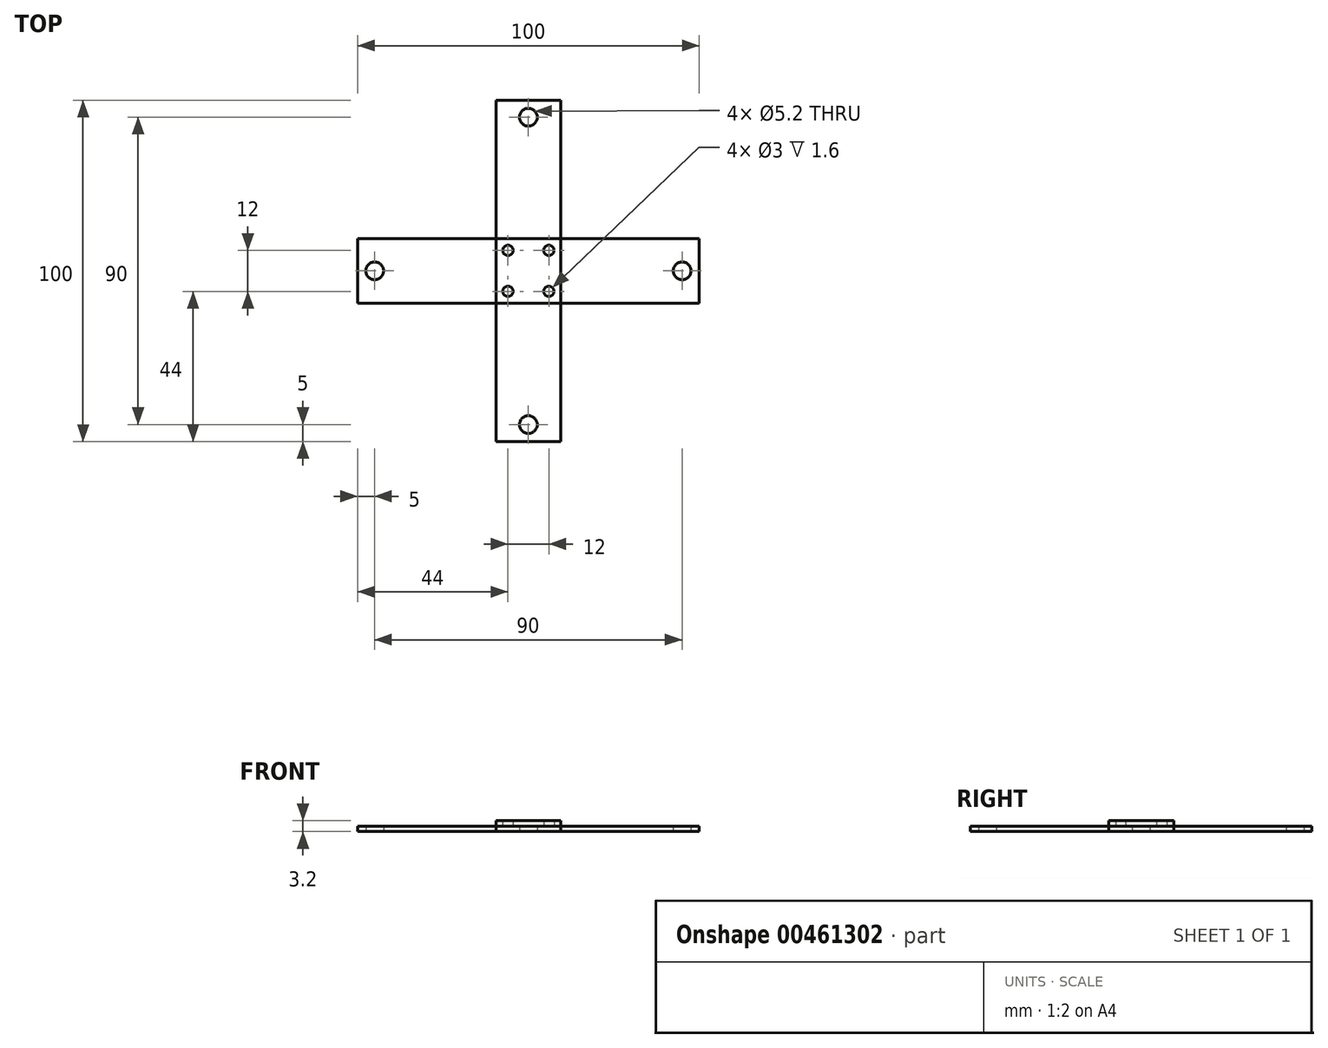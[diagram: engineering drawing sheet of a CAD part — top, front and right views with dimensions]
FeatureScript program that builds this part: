
annotation { "Feature Type Name" : "Feature", "Feature Type Description" : "" }
export const myFeature = defineFeature(function(context is Context, id is Id, definition is map)
    precondition{}
    {
        {
            var Q0;
            Q0=qCreatedBy(makeId("Top.planeOp"),FACE);
            var sketch = newSketch(context, id + "F0", { "sketchPlane" : qUnion([Q0])});
            skLineSegment(sketch, "E0", {"start": v(-9.5, 50) * mm, "end": v(9.5, 50) * mm});
            skLineSegment(sketch, "E1", {"start": v(9.5, 50) * mm, "end": v(9.5, 9.5) * mm});
            skLineSegment(sketch, "E2", {"start": v(9.5, 9.5) * mm, "end": v(50, 9.5) * mm});
            skLineSegment(sketch, "E3", {"start": v(50, 9.5) * mm, "end": v(50, -9.5) * mm});
            skLineSegment(sketch, "E4", {"start": v(50, -9.5) * mm, "end": v(9.5, -9.5) * mm});
            skLineSegment(sketch, "E5", {"start": v(9.5, -9.5) * mm, "end": v(9.5, -50) * mm});
            skLineSegment(sketch, "E6", {"start": v(9.5, -50) * mm, "end": v(-9.5, -50) * mm});
            skLineSegment(sketch, "E7", {"start": v(-9.5, -50) * mm, "end": v(-9.5, -9.5) * mm});
            skLineSegment(sketch, "E8", {"start": v(-9.5, -9.5) * mm, "end": v(-50, -9.5) * mm});
            skLineSegment(sketch, "E9", {"start": v(-50, -9.5) * mm, "end": v(-50, 9.5) * mm});
            skLineSegment(sketch, "E10", {"start": v(-50, 9.5) * mm, "end": v(-9.5, 9.5) * mm});
            skLineSegment(sketch, "E11", {"start": v(-9.5, 9.5) * mm, "end": v(-9.5, 50) * mm});
            skCircle(sketch, "E12", {"center": v(0, 45) * mm, "radius": 2.6 * mm});
            skLineSegment(sketch, "E13", {"start": v(0, 103.68) * mm, "end": v(0, -13.68) * mm, "construction": true});
            skPoint(sketch, "E13.endSnap0", {"position": v(0, -50) * mm});
            skLineSegment(sketch, "E14", {"start": v(-57.87, 0) * mm, "end": v(56.03, 0) * mm, "construction": true});
            skCircle(sketch, "E15.1.0", {"center": v(45, 0) * mm, "radius": 2.6 * mm});
            skCircle(sketch, "E15.2.0", {"center": v(0, -45) * mm, "radius": 2.6 * mm});
            skCircle(sketch, "E15.3.0", {"center": v(-45, 0) * mm, "radius": 2.6 * mm});
            skPoint(sketch, "E15.center", {"position": v(0, 0) * mm});
            skLineSegment(sketch, "E15.anchor1", {"start": v(0, 0) * mm, "end": v(0, 45) * mm, "construction": true});
            skLineSegment(sketch, "E15.anchor2", {"start": v(0, 0) * mm, "end": v(-45, 0) * mm, "construction": true});
            skCircle(sketch, "E16", {"center": v(6, 6) * mm, "radius": 1.5 * mm});
            skCircle(sketch, "E17.1.0", {"center": v(-6, 6) * mm, "radius": 1.5 * mm});
            skCircle(sketch, "E17.2.0", {"center": v(-6, -6) * mm, "radius": 1.5 * mm});
            skCircle(sketch, "E17.3.0", {"center": v(6, -6) * mm, "radius": 1.5 * mm});
            skLineSegment(sketch, "E18.bottom", {"start": v(-9.5, 9.5) * mm, "end": v(9.5, 9.5) * mm});
            skLineSegment(sketch, "E18.top", {"start": v(-9.5, 9.5) * mm, "end": v(9.5, 9.5) * mm});
            skLineSegment(sketch, "E18.left", {"start": v(-9.5, 9.5) * mm, "end": v(-9.5, 9.5) * mm});
            skLineSegment(sketch, "E18.right", {"start": v(9.5, 9.5) * mm, "end": v(9.5, 9.5) * mm});
            skLineSegment(sketch, "E19.top", {"start": v(9.5, -9.5) * mm, "end": v(9.5, -9.5) * mm});
            skLineSegment(sketch, "E19.left", {"start": v(9.5, 9.5) * mm, "end": v(9.5, -9.5) * mm});
            skLineSegment(sketch, "E19.right", {"start": v(9.5, 9.5) * mm, "end": v(9.5, -9.5) * mm});
            skLineSegment(sketch, "E20.bottom", {"start": v(9.5, -9.5) * mm, "end": v(-9.5, -9.5) * mm});
            skLineSegment(sketch, "E20.top", {"start": v(9.5, -9.5) * mm, "end": v(-9.5, -9.5) * mm});
            skLineSegment(sketch, "E20.right", {"start": v(-9.5, -9.5) * mm, "end": v(-9.5, -9.5) * mm});
            skLineSegment(sketch, "E21.left", {"start": v(-9.5, -9.5) * mm, "end": v(-9.5, 9.5) * mm});
            skLineSegment(sketch, "E21.right", {"start": v(-9.5, -9.5) * mm, "end": v(-9.5, 9.5) * mm});
            skSolve(sketch);
        }
        {
            var Q0;
            Q0=makeQuery(id+"F0.imprint","IMPRINT",FACE,{"disambiguationData":[TD([[makeQuery(id+"F0.imprint","IMPRINT",EDGE,{"derivedFrom":sQuery(id+"F0.wireOp",EDGE,"E8")}),-1.0]])]});
            var Q1;
            Q1=makeQuery(id+"F0.imprint","IMPRINT",FACE,{"disambiguationData":[TD([[makeQuery(id+"F0.imprint","IMPRINT",EDGE,{"derivedFrom":sQuery(id+"F0.wireOp",EDGE,"E0")}),-1.0]])]});
            var Q2;
            Q2=makeQuery(id+"F0.imprint","IMPRINT",FACE,{"disambiguationData":[TD([[makeQuery(id+"F0.imprint","IMPRINT",EDGE,{"derivedFrom":sQuery(id+"F0.wireOp",EDGE,"E2")}),-1.0]])]});
            var Q3;
            Q3=makeQuery(id+"F0.imprint","IMPRINT",FACE,{"disambiguationData":[TD([[makeQuery(id+"F0.imprint","IMPRINT",EDGE,{"derivedFrom":sQuery(id+"F0.wireOp",EDGE,"E5")}),-1.0]])]});
            extrude(context, id + "F1", {"entities" : qUnion([Q0, Q1, Q2, Q3]), "depth" : 1.6 * mm, "offsetDistance" : 25 * mm});
        }
        {
            var Q0;
            Q0=makeQuery(id+"F0.imprint","IMPRINT",FACE,{"disambiguationData":[TD([[makeQuery(id+"F0.imprint","IMPRINT",EDGE,{"derivedFrom":sQuery(id+"F0.wireOp",EDGE,"E16")}),-1.0]])]});
            extrude(context, id + "F2", {"entities" : qUnion([Q0]), "depth" : 3.2 * mm, "offsetDistance" : 25 * mm});
        }
        {
            var Q0;
            Q0=makeQuery(id+"F0.imprint","IMPRINT",FACE,{"disambiguationData":[TD([[makeQuery(id+"F0.imprint","IMPRINT",EDGE,{"derivedFrom":sQuery(id+"F0.wireOp",EDGE,"E17.3.0")}),1.0]])]});
            var Q1;
            Q1=makeQuery(id+"F0.imprint","IMPRINT",FACE,{"disambiguationData":[TD([[makeQuery(id+"F0.imprint","IMPRINT",EDGE,{"derivedFrom":sQuery(id+"F0.wireOp",EDGE,"E16")}),1.0]])]});
            var Q2;
            Q2=makeQuery(id+"F0.imprint","IMPRINT",FACE,{"disambiguationData":[TD([[makeQuery(id+"F0.imprint","IMPRINT",EDGE,{"derivedFrom":sQuery(id+"F0.wireOp",EDGE,"E17.1.0")}),1.0]])]});
            var Q3;
            Q3=makeQuery(id+"F0.imprint","IMPRINT",FACE,{"disambiguationData":[TD([[makeQuery(id+"F0.imprint","IMPRINT",EDGE,{"derivedFrom":sQuery(id+"F0.wireOp",EDGE,"E17.2.0")}),1.0]])]});
            extrude(context, id + "F3", {"entities" : qUnion([Q0, Q1, Q2, Q3]), "operationType" : NewBodyOperationType.ADD, "depth" : 1.6 * mm, "offsetDistance" : 25 * mm});
        }
    });
